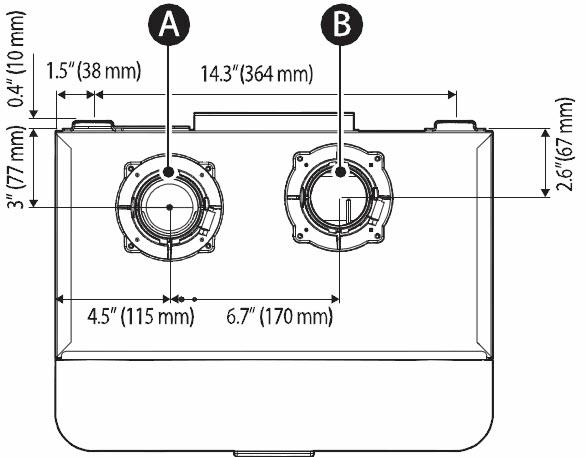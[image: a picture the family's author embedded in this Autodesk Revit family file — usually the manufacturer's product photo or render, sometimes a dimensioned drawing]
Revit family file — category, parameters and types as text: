
# Revit family: Water_Heater-Racks-Navien-NPE-15_Unit_Back_to_Back---
name_source: partatom
category: Mechanical Equipment
revit_build: Autodesk Revit 2016 (Build: 20150220_1215(x64)
units: mm (PartAtom-declared; Revit-internal decimal feet)

## family parameters
Cut with Voids When Loaded = No
Host = Face
OmniClass Number = 23.65.35.11
OmniClass Title = Supply Water Heaters
Part Type = Normal
Room Calculation Point = No
Round Connector Dimension = Use Diameter
Shared = No

## types (4) — shared parameters
2" Exhaust/Intake = Yes
3" Exhaust/Intake = No
Apparent Load = 0 VA
Assembly Code = D3010500
Certifications = Energy Star | AHRI | CSA | CSA | NFS
Cold Water Inlet = 1"
Configuration = NPE_B15_4B4B_4B3B
Default Elevation = 48 "
Depth = 23.8 "
Description = 15 Unit Back to Back
Exhaust = 2"
Finish = Metal - Navien - White
Flow Rate = 1 GPM
Flow Rate Note = 35°F (19°C) temp rise: 11.2 GPM (42 L/m) | 45°F (25°C) temp rise: 8.7 GPM (33 L/m) | 67°F (36°C) temp rise: NPE-240A: 5.6 GPM(21 L/m), NPE-240S: 5.7 GPM(22 L/m)
Frequency = 60 Hz
Gas Inlet = 1"
Heating Capacity = 120000.0 Btu/h
Heating Capacity Note = 19,900–199,900 (BTU/H)
Height = 65.5 "
Hot Water Outlet = 1"
Ignition = Electronic ignition
Installation Type = Indoor
Intake = 2"
Keynote = 22 33 00.A1
Manifold(s) = (4) 30019042A
Manufacturer = Navien, Inc.
Manufacturer Fax Number = (949) 420-0430
Natural Gas Manifold Pressure = -0.05" WC to -0.58" WC
Natural Gas Supply Pressure = 3.5"–10.5" WC
Number of Poles = 1
Phase = 1
Power Factor = 1
Product Documentation Link = https://www.navieninc.com
Product Name = NPE Series Tankless Water Heaters w/ Racks
Product Page URL = https://www.navieninc.com
Propane Gas Manifold Pressure = -0.10" WC to -0.78" WC
Propane Gas Supply Pressure = 8"–13" WC
Rack(s) = (2) GFFM-KDIZUS-003 + (6) GFFM-KDIZUS-004
Required Cascade Operation Accessory = (15) 30014367A (Common Vent Damper & Cascade Communication Cable) or (14) GXXX000546 (Individual Vent Cascade Communication Cable)
URL = https://www.navieninc.com
Venting = Exhaust: 2" PVC, CPVC, PP, SS / 2" special gas vent type BH (Class II, A/B/C) | Intake: 2" PVC, CPVC, PP, SS / 2" special gas vent type BH (Class II, A/B/C) | Vent clearances: 0" to combustibles
Venting Type = Forced draft direct vent
Version = 2016 - v1.0.a
Voltage = 120 V
Water Pressure = 15–150 PSI
Wi-Fi Ready = NaviLink Wi-Fi Control: PBCM-AS-001
Width = 182.3 "

## per-type parameters (varying)
| type | Constraints | Model | Natural Gas | Propane Gas | Recirculation Inlet | Recirculation Inlet Visibility | Tankless Water Heaters | Weight |
| Natural Gas - Recirculating System - NPE-240A(Advanced)-NG | 6 | (15) NPE-240A-NG | Yes | No | 0" | Yes | (15) NPE-240A-NG | 82.00 lbf |
| Natural Gas - NPE-240S(Standard)-NG | 7 | (15) NPE-240S-NG | Yes | No | 1" | No | (15) NPE-240S-NG | 75.00 lbf |
| Propane Gas - Recirculating System - NPE-240A(Advanced)-LPG | 6 | (15) NPE-240A-LPG | No | Yes | 0" | Yes | (15) NPE-240A-LPG | 82.00 lbf |
| Propane Gas - NPE-240S(Standard)-LPG | 7 | (15) NPE-240S-LPG | No | Yes | 1" | No | (15) NPE-240S-LPG | 75.00 lbf |

## geometry (parser evidence)
native form markers: Sweep x22
no freeform markers — native parametric forms only
